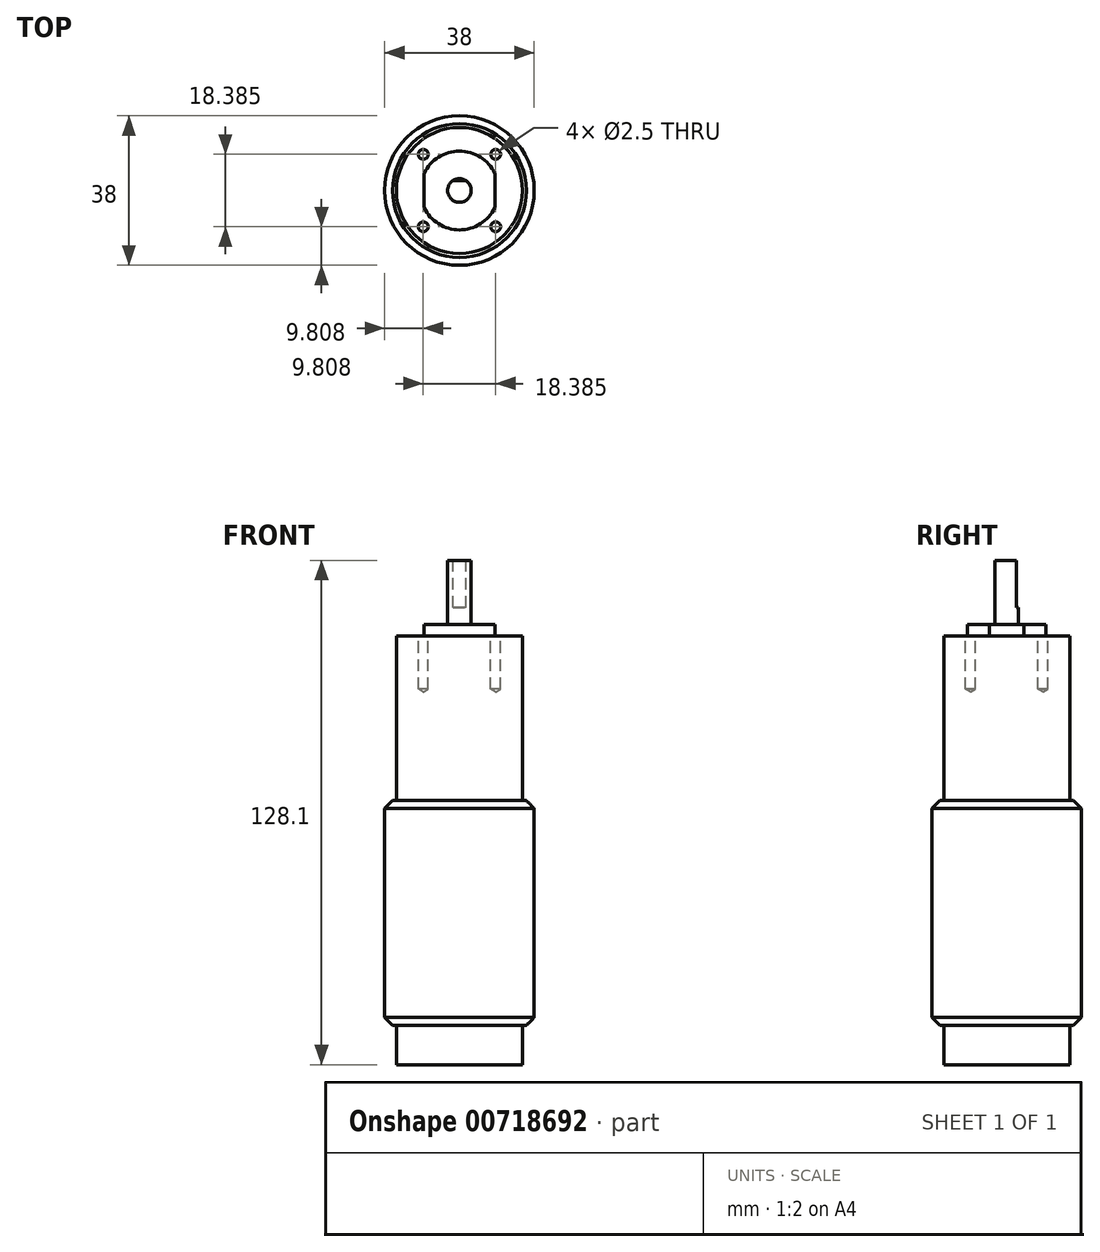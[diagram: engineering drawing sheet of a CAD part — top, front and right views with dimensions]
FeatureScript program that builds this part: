
annotation { "Feature Type Name" : "Feature", "Feature Type Description" : "" }
export const myFeature = defineFeature(function(context is Context, id is Id, definition is map)
    precondition{}
    {
        {
            var Q0;
            Q0=qCreatedBy(makeId("Top.planeOp"),FACE);
            var sketch = newSketch(context, id + "F0", { "sketchPlane" : qUnion([Q0])});
            skCircle(sketch, "E0", {"center": v(0, 0) * mm, "radius": 19 * mm});
            skSolve(sketch);
        }
        {
            var Q0;
            Q0 = qSketchRegion(id + "F0", true);
            extrude(context, id + "F1", {"entities" : qUnion([Q0]), "oppositeDirection" : true, "depth" : 57.1 * mm, "offsetDistance" : 25 * mm});
        }
        {
            var Q0;
            Q0=makeQuery(id+"F1.opExtrude","CAP_FACE",FACE,{"disambiguationData":[OSD([sQuery(id+"F0.wireOp",EDGE,"E0")])],"isStart":true});
            var sketch = newSketch(context, id + "F2", { "sketchPlane" : qUnion([Q0])});
            skCircle(sketch, "E1", {"center": v(0, 0) * mm, "radius": 16 * mm});
            skSolve(sketch);
        }
        {
            var Q0;
            Q0 = qSketchRegion(id + "F2", true);
            extrude(context, id + "F3", {"entities" : qUnion([Q0]), "operationType" : NewBodyOperationType.ADD, "depth" : 41.8 * mm, "offsetDistance" : 25 * mm});
        }
        {
            var Q0;
            Q0=makeQuery(id+"F1.opExtrude","CAP_FACE",FACE,{"disambiguationData":[OSD([sQuery(id+"F0.wireOp",EDGE,"E0")])],"isStart":false});
            var sketch = newSketch(context, id + "F4", { "sketchPlane" : qUnion([Q0])});
            skCircle(sketch, "E2", {"center": v(0, 0) * mm, "radius": 16 * mm});
            skSolve(sketch);
        }
        {
            var Q0;
            Q0 = qSketchRegion(id + "F4", true);
            extrude(context, id + "F5", {"entities" : qUnion([Q0]), "operationType" : NewBodyOperationType.ADD, "depth" : 10 * mm, "offsetDistance" : 25 * mm});
        }
        {
            var Q0;
            Q0=makeQuery(id+"F3.opExtrude","CAP_FACE",FACE,{"disambiguationData":[OSD([sQuery(id+"F2.wireOp",EDGE,"E1")])],"isStart":false});
            var sketch = newSketch(context, id + "F6", { "sketchPlane" : qUnion([Q0])});
            skCircle(sketch, "E3", {"center": v(0, 0) * mm, "radius": 10 * mm, "construction": true});
            skLineSegment(sketch, "E4.bottom", {"start": v(-9, 4.36) * mm, "end": v(9, 4.36) * mm, "construction": true});
            skLineSegment(sketch, "E4.top", {"start": v(-9, -4.36) * mm, "end": v(9, -4.36) * mm, "construction": true});
            skLineSegment(sketch, "E4.left", {"start": v(-9, 4.36) * mm, "end": v(-9, -4.36) * mm});
            skLineSegment(sketch, "E4.right", {"start": v(9, 4.36) * mm, "end": v(9, -4.36) * mm});
            skArc(sketch, "E5", {"start": v(-9, 4.36) * mm, "mid": v(0, 10) * mm, "end": v(9, 4.36) * mm});
            skArc(sketch, "E6", {"start": v(-9, -4.36) * mm, "mid": v(0, -10) * mm, "end": v(9, -4.36) * mm});
            skSolve(sketch);
        }
        {
            var Q0;
            Q0 = qSketchRegion(id + "F6", true);
            extrude(context, id + "F7", {"entities" : qUnion([Q0]), "operationType" : NewBodyOperationType.ADD, "depth" : 3 * mm, "offsetDistance" : 25 * mm});
        }
        {
            var Q0;
            Q0=makeQuery(id+"F7.opExtrude","CAP_FACE",FACE,{"disambiguationData":[OSD([sQuery(id+"F6.wireOp",EDGE,"E4.left"),sQuery(id+"F6.wireOp",EDGE,"E4.right"),sQuery(id+"F6.wireOp",EDGE,"E5"),sQuery(id+"F6.wireOp",EDGE,"E6")])],"isStart":false});
            var sketch = newSketch(context, id + "F8", { "sketchPlane" : qUnion([Q0])});
            skCircle(sketch, "E7", {"center": v(0, 0) * mm, "radius": 3 * mm});
            skSolve(sketch);
        }
        {
            var Q0;
            Q0 = qSketchRegion(id + "F8", true);
            extrude(context, id + "F9", {"entities" : qUnion([Q0]), "operationType" : NewBodyOperationType.ADD, "depth" : (19.2 - 3) * mm, "offsetDistance" : 25 * mm});
        }
        {
            var Q0;
            Q0=makeQuery(id+"F9.opExtrude","CAP_FACE",FACE,{"disambiguationData":[OSD([sQuery(id+"F8.wireOp",EDGE,"E7")])],"isStart":false});
            var sketch = newSketch(context, id + "F10", { "sketchPlane" : qUnion([Q0])});
            skLineSegment(sketch, "E8.bottom", {"start": v(-1.66, 2.5) * mm, "end": v(1.66, 2.5) * mm});
            skLineSegment(sketch, "E8.top", {"start": v(-1.66, 3) * mm, "end": v(1.66, 3) * mm});
            skLineSegment(sketch, "E8.left", {"start": v(-1.66, 2.5) * mm, "end": v(-1.66, 3) * mm});
            skLineSegment(sketch, "E8.right", {"start": v(1.66, 2.5) * mm, "end": v(1.66, 3) * mm});
            skCircle(sketch, "E9.0", {"center": v(0, 0) * mm, "radius": 3 * mm, "construction": true});
            skSolve(sketch);
        }
        {
            var Q0;
            Q0 = qSketchRegion(id + "F10", true);
            extrude(context, id + "F11", {"entities" : qUnion([Q0]), "operationType" : NewBodyOperationType.REMOVE, "oppositeDirection" : true, "depth" : 12 * mm, "offsetDistance" : 25 * mm});
        }
        {
            var Q0;
            Q0=makeQuery(id+"F1.opExtrude","CAP_EDGE",EDGE,{"disambiguationData":[OSD([sQuery(id+"F0.wireOp",EDGE,"E0")])],"isStart":false});
            var Q1;
            Q1=makeQuery(id+"F1.opExtrude","CAP_EDGE",EDGE,{"disambiguationData":[OSD([sQuery(id+"F0.wireOp",EDGE,"E0")])],"isStart":true});
            chamfer(context, id + "F12", {"entities" : qUnion([Q0, Q1]), "width" : 2 * mm, "tangentPropagation" : true});
        }
        {
            var Q0;
            Q0=makeQuery(id+"F3.opExtrude","CAP_FACE",FACE,{"disambiguationData":[OSD([sQuery(id+"F2.wireOp",EDGE,"E1")])],"isStart":false});
            var sketch = newSketch(context, id + "F13", { "sketchPlane" : qUnion([Q0])});
            skLineSegment(sketch, "E10.bottom", {"start": v(-9.2, 9.2) * mm, "end": v(9.2, 9.2) * mm, "construction": true});
            skLineSegment(sketch, "E10.top", {"start": v(-9.2, -9.2) * mm, "end": v(9.2, -9.2) * mm, "construction": true});
            skLineSegment(sketch, "E10.left", {"start": v(-9.2, 9.2) * mm, "end": v(-9.2, -9.2) * mm, "construction": true});
            skLineSegment(sketch, "E10.right", {"start": v(9.2, 9.2) * mm, "end": v(9.2, -9.2) * mm, "construction": true});
            skLineSegment(sketch, "E11", {"start": v(-9.2, 9.2) * mm, "end": v(9.2, -9.2) * mm, "construction": true});
            skCircle(sketch, "E12", {"center": v(0, 0) * mm, "radius": 13 * mm, "construction": true});
            skSolve(sketch);
        }
        {
            var Q0;
            Q0=sQuery(id+"F13.wireOp",VERTEX,"E10.bottom.start");
            var Q1;
            Q1=sQuery(id+"F13.wireOp",VERTEX,"E10.right.start");
            var Q2;
            Q2=sQuery(id+"F13.wireOp",VERTEX,"E10.top.end");
            var Q3;
            Q3=sQuery(id+"F13.wireOp",VERTEX,"E10.left.end");
            var Q4;
            Q4=makeQuery(id+"F1.opExtrude","SWEPT_BODY",BODY,{"disambiguationData":[OSD([sQuery(id+"F0.wireOp",EDGE,"E0")])]});
            hole(context, id + "F14", {"style" : HoleStyle.SIMPLE, "endStyle" : HoleEndStyle.BLIND, "standardTappedOrClearance" : lookupTablePath({ "standard" : "ISO", "engagement" : "75%", "pitch" : "0.5 mm", "size" : "M3", "type" : "Tapped" }), "standardBlindInLast" : lookupTablePath({ "standard" : "ISO", "engagement" : "75%", "pitch" : "0.5 mm", "size" : "M3", "type" : "Tapped" }), "holeDiameter" : 2.5 * mm, "majorDiameter" : 3 * mm, "showTappedDepth" : true, "holeDepth" : 13.5 * mm, "isTappedThrough" : true, "tappedDepth" : 12 * mm, "tapClearance" : 3, "startFromSketch" : true, "locations" : qUnion([Q0, Q1, Q2, Q3]), "scope" : qUnion([Q4])});
        }
    });
